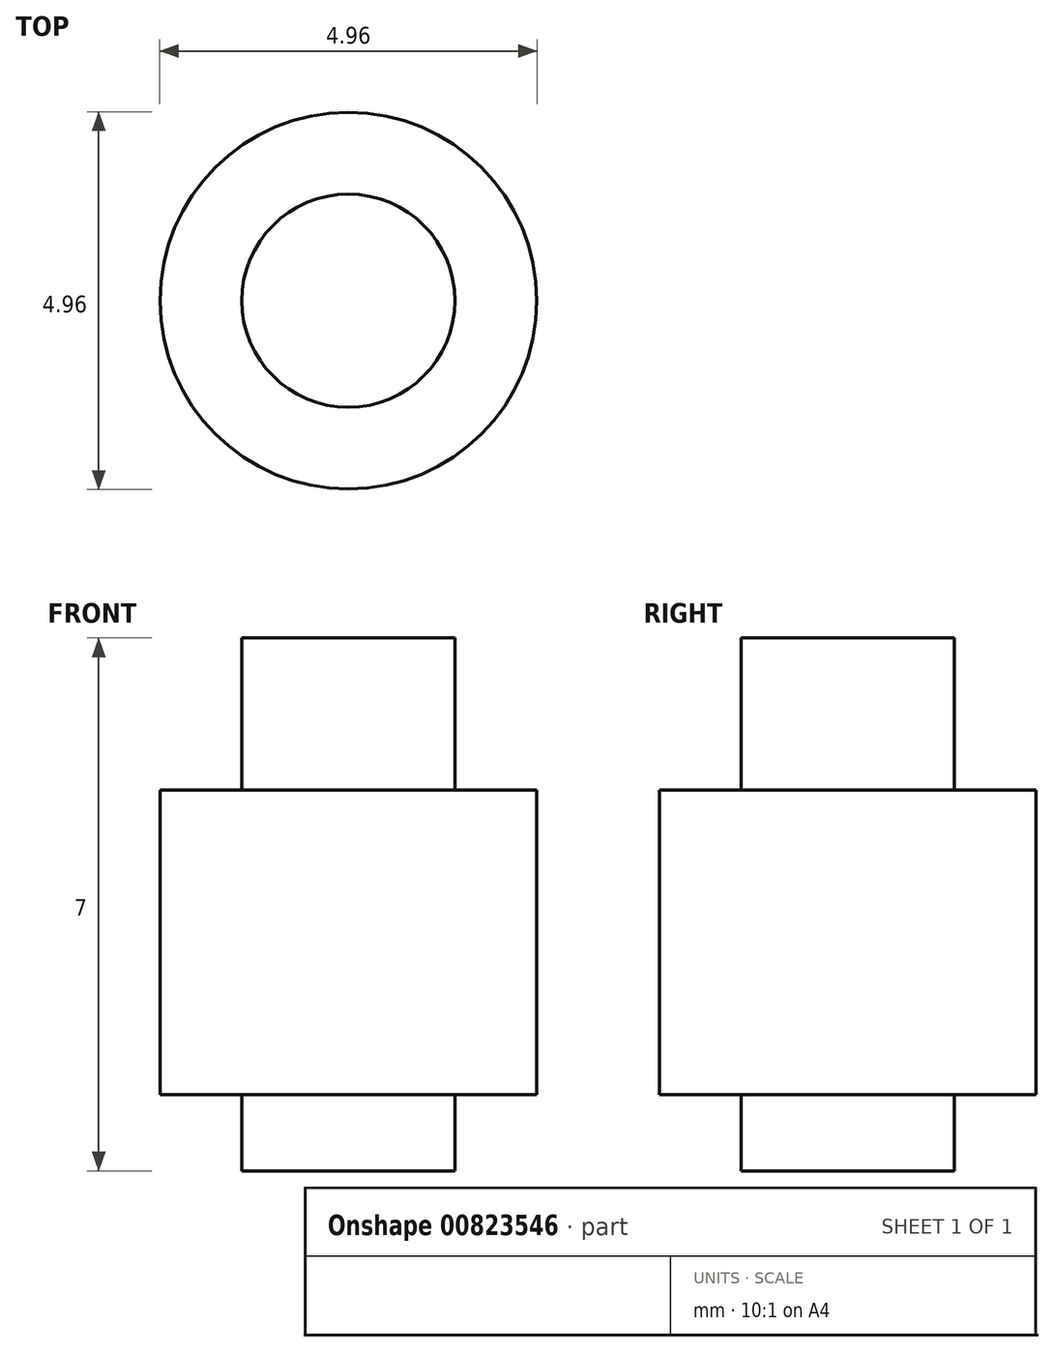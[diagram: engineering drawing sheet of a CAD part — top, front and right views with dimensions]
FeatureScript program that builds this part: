
annotation { "Feature Type Name" : "Feature", "Feature Type Description" : "" }
export const myFeature = defineFeature(function(context is Context, id is Id, definition is map)
    precondition{}
    {
        {
            var Q0;
            Q0=qCreatedBy(makeId("Top.planeOp"),FACE);
            var sketch = newSketch(context, id + "F0", { "sketchPlane" : qUnion([Q0])});
            skCircle(sketch, "E0", {"center": v(0, 0) * mm, "radius": 1.5 * mm});
            skCircle(sketch, "E1", {"center": v(0, 0) * mm, "radius": 2.48 * mm});
            skSolve(sketch);
        }
        {
            var Q0;
            Q0=makeQuery(id+"F0.imprint","IMPRINT",FACE,{"disambiguationData":[TD([[makeQuery(id+"F0.imprint","IMPRINT",EDGE,{"derivedFrom":sQuery(id+"F0.wireOp",EDGE,"E0")}),-1.0]])]});
            var Q1;
            Q1=makeQuery(id+"F0.imprint","IMPRINT",FACE,{"disambiguationData":[TD([[makeQuery(id+"F0.imprint","IMPRINT",EDGE,{"derivedFrom":sQuery(id+"F0.wireOp",EDGE,"E0")}),1.0]])]});
            extrude(context, id + "F1", {"entities" : qUnion([Q0, Q1]), "depth" : 4 * mm, "offsetDistance" : 25 * mm});
        }
        {
            var Q0;
            Q0=makeQuery(id+"F1.opExtrude","CAP_FACE",FACE,{"disambiguationData":[OSD([sQuery(id+"F0.wireOp",EDGE,"E1")])],"isStart":false});
            var sketch = newSketch(context, id + "F2", { "sketchPlane" : qUnion([Q0])});
            skCircle(sketch, "E2", {"center": v(0, 0) * mm, "radius": 1.4 * mm});
            skSolve(sketch);
        }
        {
            var Q0;
            Q0=makeQuery(id+"F2.imprint","IMPRINT",FACE,{"disambiguationData":[TD([[makeQuery(id+"F2.imprint","IMPRINT",EDGE,{"derivedFrom":sQuery(id+"F2.wireOp",EDGE,"E2")}),1.0]])]});
            extrude(context, id + "F3", {"entities" : qUnion([Q0]), "operationType" : NewBodyOperationType.ADD, "depth" : 2 * mm, "offsetDistance" : 25 * mm});
        }
        {
            var Q0;
            Q0=makeQuery(id+"F1.opExtrude","CAP_FACE",FACE,{"disambiguationData":[OSD([sQuery(id+"F0.wireOp",EDGE,"E1")])],"isStart":true});
            var sketch = newSketch(context, id + "F4", { "sketchPlane" : qUnion([Q0])});
            skCircle(sketch, "E3", {"center": v(0, 0) * mm, "radius": 1.4 * mm});
            skSolve(sketch);
        }
        {
            var Q0;
            Q0=makeQuery(id+"F4.imprint","IMPRINT",FACE,{"disambiguationData":[TD([[makeQuery(id+"F4.imprint","IMPRINT",EDGE,{"derivedFrom":sQuery(id+"F4.wireOp",EDGE,"E3")}),1.0]])]});
            extrude(context, id + "F5", {"entities" : qUnion([Q0]), "operationType" : NewBodyOperationType.ADD, "depth" : 1 * mm, "offsetDistance" : 25 * mm});
        }
    });
